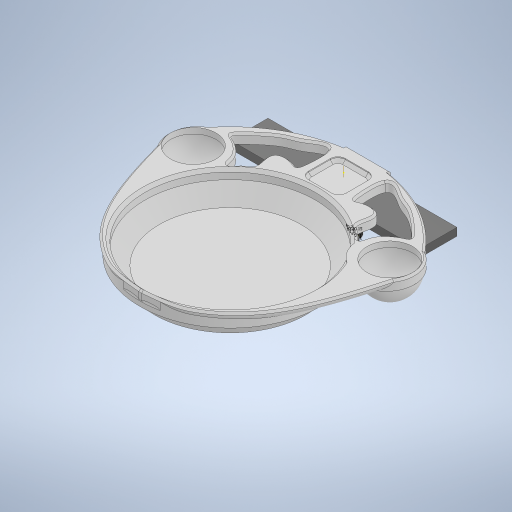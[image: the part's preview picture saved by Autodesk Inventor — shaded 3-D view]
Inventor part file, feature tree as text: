
AUTODESK INVENTOR PART (.ipt)
format: ipt  version: 2024.1 (Build 281209000, 209)  size: 1,651,712 bytes
history: native  units: mm
features: extrude x18, projected_geometry x15, sketch x11, chamfer x11, fillet x9, helix x2, other x2, hole x1, plane x1, thread x1, pattern_circular x1, mirror x1, revolve x1
ambient origin geometry x8: Origin, YZ Plane, XZ Plane, XY Plane, X Axis, Y Axis, Z Axis, Center Point
bodies: Solid1 (feature_tree)
feature tree (74):
  extrude  "Extrusion1"  Depth=40.0mm
  extrude  "Extrusion2"  Depth=20.0mm
  extrude  "Extrusion3"  Depth=45.0mm
  extrude  "Extrusion4"  Depth=10.0mm
  extrude  "Extrusion5"  Depth=10.0mm TaperAngle=0.0deg
  hole  "Hole1"  [1 undecoded]
  plane  "Work Plane1"
  extrude  "Extrusion6"  Depth=10.0mm TaperAngle=0.0deg
  extrude  "Extrusion7"  Depth=2.0mm
  extrude  "Extrusion20"  Depth=10.0mm TaperAngle=0.0deg
  sketch  "Sketch24"  dims[d19=12.0mm]
  helix  "Coil1"  [1 undecoded]
  helix  "Coil2"  [1 undecoded]
  chamfer  "Chamfer8"  Distance=30.0mm
  chamfer  "Chamfer9"  Distance=2.0mm Angle=45.0deg
  thread  "Thread1"  [1 undecoded]
  fillet  "Fillet1"  [1 undecoded]
  chamfer  "Chamfer1"  Distance=60.0mm Angle=360.0deg
  extrude  "Extrusion8"  Depth=10.0mm
  pattern_circular  "Circular Pattern1"  Count=18  [1 undecoded]
  fillet  "Fillet2"  Radius=90.0mm
  extrude  "Extrusion9"  Depth=10.0mm
  sketch  "Sketch13"  dims[d2=100.0mm d3=20.0mm]
  extrude  "Extrusion18"  Depth=10.0mm
  extrude  "Extrusion19"  Depth=10.0mm
  chamfer  "Chamfer5"  Distance=100.0mm
  chamfer  "Chamfer10"  Distance=50.0mm
  fillet  "Fillet17"  Radius=50.0mm
  extrude  "Extrusion11"  Depth=10.0mm TaperAngle=0.0deg
  chamfer  "Chamfer2"  Distance=3.0mm
  fillet  "Fillet8"  Radius=50.0mm
  chamfer  "Chamfer3"  Distance=2.0mm Angle=45.0deg
  fillet  "Fillet9"  Radius=10.0mm
  chamfer  "Chamfer11"  Distance=2.0mm Angle=45.0deg
  extrude  "Extrusion14"  Depth=10.0mm
  mirror  "Mirror1"
  extrude  "Extrusion15"  Depth=10.0mm
  revolve  "Revolution1"  [1 undecoded]
  fillet  "Fillet11"  Radius=13.0mm
  chamfer  "Chamfer12"  Distance=138.0mm
  extrude  "Extrusion16"  TaperAngle=0.0deg  [1 undecoded]
  extrude  "Extrusion17"  Depth=10.0mm
  fillet  "Fillet13"  Radius=20.057674mm
  fillet  "Fillet14"  Radius=25.0mm
  chamfer  "Chamfer4"  Distance=4.0mm
  fillet  "Fillet16"  Radius=8.0mm
  chamfer  "Chamfer13"  Distance=20.0mm
  extrude  "Extrusion21"  Depth=10.0mm TaperAngle=0.0deg
  other  "clamp"
  projected_geometry  "Projected Loop1"
  projected_geometry  "Projected Loop2"
  projected_geometry  "Projected Loop3"
  other  "screw"
  projected_geometry  "Projected Loop5"
  sketch  "Sketch12"  dims[d0=200.0mm d1=40.0mm]
  projected_geometry  "Projected Loop6"
  projected_geometry  "Projected Loop7"
  sketch  "Sketch17"  dims[d4=8.2mm d5=0.0mm d6=45.0mm]
  projected_geometry  "Projected Loop12"
  sketch  "Sketch20"  dims[d7=22.5mm d8=10.0mm]
  projected_geometry  "Projected Loop13"
  sketch  "Sketch21"  dims[d9=10.0mm d10=10.0mm d11=0.0mm]
  projected_geometry  "Projected Loop15"
  projected_geometry  "Projected Loop16"
  sketch  "Sketch22"  dims[d12=10.0mm d13=0.0mm d14=20.0mm d15=0.0mm]
  sketch  "Sketch23"  dims[d16=39.0mm d17=10.0mm d18=0.0mm]
  projected_geometry  "Projected Loop18"
  projected_geometry  "Projected Loop19"
  sketch  "Sketch25"  dims[d20=12.0mm d21=24.0mm d22=3.023mm d23=2.0mm d24=90.0deg d25=32.3mm d26=0.0mm d27=15.0mm]
  projected_geometry  "Projected Loop20"
  sketch  "Sketch26"  dims[d28=30.0mm d29=10.0mm d30=0.0mm d32=12.0mm d33=27.0mm d34=0.0mm d35=30.0mm d36=0.0mm]
  sketch  "Sketch27"  dims[d37=2.0mm d38=2.0mm d39=2.0mm d40=45.0deg d41=8.5mm d42=0.0mm d43=0.0mm d44=60.0mm d45=360.0deg d47=3.0mm d48=180.0mm d49=90.0mm d51=60.0mm d52=35.0mm d53=100.0mm d54=100.0mm d55=50.0mm d56=50.0mm d57=10.0mm d58=0.0mm d59=3.0mm d65=50.0mm d66=0.0mm d71=2.0mm d72=2.0mm d73=45.0deg d74=10.0mm d75=5.0mm d76=2.0mm d77=45.0deg d78=27.0mm d87=13.0mm d88=13.0mm d89=13.0mm d90=138.0mm d92=0.0mm d93=0.0mm d97=20.057674mm d98=20.057674mm d99=25.0mm d100=4.0mm d101=0.0mm d102=8.0mm d104=20.0mm d105=0.0mm d106=3.0mm d107=0.0mm d108=24.0mm d109=25.0mm d111=2.0mm d112=2.0mm d113=45.0deg d114=14.0mm d115=40.115347mm d116=1.7mm d119=15.0mm d120=0.0mm d121=5.0mm d122=0.0mm d123=15.0mm d124=2.0mm d125=45.0deg d129=6.0mm d133=2.0mm d135=1.0mm d136=2.4mm d137=20.0mm d138=10.0mm d139=0.0mm d140=90.0deg d141=90.0deg d142=0.0mm d143=0.0mm d144=2.5mm d145=25.0mm d146=10.0mm d147=0.0mm d148=90.0deg d149=90.0deg d150=0.0mm d151=0.0mm d152=0.15mm d156=0.2mm d157=0.2mm d158=1.5mm d159=1.5mm d160=5.0mm d161=0.0mm d162=0.5mm d163=2.0mm d164=45.0deg d165=0.5mm d166=2.0mm d167=45.0deg d168=3.0mm d169=2.0mm d170=45.0deg d171=20.0mm d172=3.0mm d173=2.0mm d174=45.0deg d175=1.0mm d176=4.0mm d177=1.5mm d178=6.0mm d179=360.0deg d180=3.0mm d181=2.0mm d182=45.0deg d183=3.0mm d184=2.0mm d185=45.0deg d186=2.0mm d187=10.0mm d188=0.0mm]
  projected_geometry  "Projected Loop21"
  projected_geometry  "Projected Loop22"
note: 8 required parameter values undecoded (feature->parameter linkage not recoverable at this tier; creation-order binding heuristic only, values carry confidence <= 0.55)